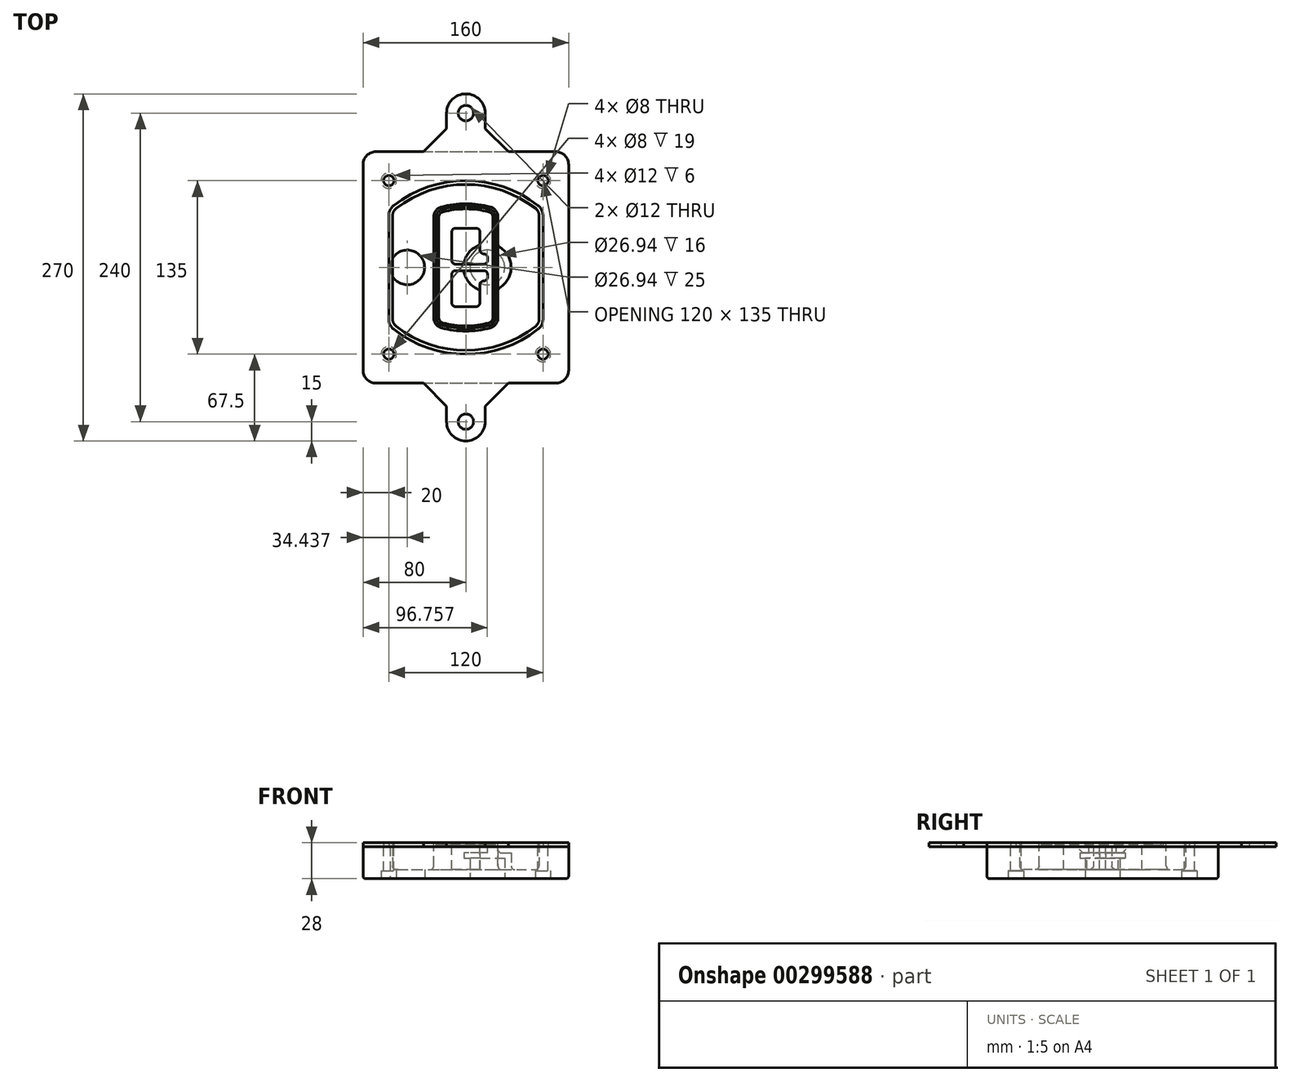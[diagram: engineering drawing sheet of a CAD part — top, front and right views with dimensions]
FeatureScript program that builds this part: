
annotation { "Feature Type Name" : "Feature", "Feature Type Description" : "" }
export const myFeature = defineFeature(function(context is Context, id is Id, definition is map)
    precondition{}
    {
        {
            var Q0;
            Q0=qCreatedBy(makeId("Top.planeOp"),FACE);
            var sketch = newSketch(context, id + "F0", { "sketchPlane" : qUnion([Q0])});
            skPoint(sketch, "E0.rect.middle", {"position": v(0, 0) * mm});
            skLineSegment(sketch, "E1.bottom", {"start": v(-70, -90) * mm, "end": v(70, -90) * mm});
            skLineSegment(sketch, "E1.top", {"start": v(-70, 90) * mm, "end": v(70, 90) * mm});
            skLineSegment(sketch, "E1.left", {"start": v(-80, -80) * mm, "end": v(-80, 80) * mm});
            skLineSegment(sketch, "E1.right", {"start": v(80, -80) * mm, "end": v(80, 80) * mm});
            skLineSegment(sketch, "E2", {"start": v(-80, 90) * mm, "end": v(80, -90) * mm, "construction": true});
            skLineSegment(sketch, "E3", {"start": v(80, 90) * mm, "end": v(-80, -90) * mm, "construction": true});
            skCircle(sketch, "E4", {"center": v(-60, 67.5) * mm, "radius": 4 * mm});
            skCircle(sketch, "E5", {"center": v(60, 67.5) * mm, "radius": 4 * mm});
            skCircle(sketch, "E6", {"center": v(60, -67.5) * mm, "radius": 4 * mm});
            skCircle(sketch, "E7", {"center": v(-60, -67.5) * mm, "radius": 4 * mm});
            skLineSegment(sketch, "E8", {"start": v(-60, 67.5) * mm, "end": v(60, 67.5) * mm, "construction": true});
            skLineSegment(sketch, "E9", {"start": v(60, 67.5) * mm, "end": v(60, -67.5) * mm, "construction": true});
            skLineSegment(sketch, "E10", {"start": v(60, -67.5) * mm, "end": v(-60, -67.5) * mm, "construction": true});
            skLineSegment(sketch, "E11", {"start": v(-60, -67.5) * mm, "end": v(-60, 67.5) * mm, "construction": true});
            skLineSegment(sketch, "E12", {"start": v(-60, 40.3) * mm, "end": v(-60, -40.3) * mm});
            skLineSegment(sketch, "E13", {"start": v(60, 40.3) * mm, "end": v(60, -40.3) * mm});
            skArc(sketch, "E14", {"start": v(56.15, 48.18) * mm, "mid": v(0, 67.5) * mm, "end": v(-56.15, 48.18) * mm});
            skArc(sketch, "E15", {"start": v(-56.15, -48.18) * mm, "mid": v(0, -67.5) * mm, "end": v(56.15, -48.18) * mm});
            skLineSegment(sketch, "E16", {"start": v(-60, 0) * mm, "end": v(60, 0) * mm, "construction": true});
            skPoint(sketch, "E17.visualSharp", {"position": v(-60, -45) * mm});
            skArc(sketch, "E17.filletArc", {"start": v(-60, -40.3) * mm, "mid": v(-58.99, -44.68) * mm, "end": v(-56.15, -48.18) * mm});
            skPoint(sketch, "E18.visualSharp", {"position": v(-60, 45) * mm});
            skArc(sketch, "E18.filletArc", {"start": v(-56.15, 48.18) * mm, "mid": v(-58.99, 44.68) * mm, "end": v(-60, 40.3) * mm});
            skPoint(sketch, "E19.visualSharp", {"position": v(60, 45) * mm});
            skArc(sketch, "E19.filletArc", {"start": v(60, 40.3) * mm, "mid": v(58.99, 44.68) * mm, "end": v(56.15, 48.18) * mm});
            skPoint(sketch, "E20.visualSharp", {"position": v(60, -45) * mm});
            skArc(sketch, "E20.filletArc", {"start": v(56.15, -48.18) * mm, "mid": v(58.99, -44.68) * mm, "end": v(60, -40.3) * mm});
            skPoint(sketch, "E21.visualSharp", {"position": v(-80, 90) * mm});
            skArc(sketch, "E21.filletArc", {"start": v(-70, 90) * mm, "mid": v(-77.07, 87.07) * mm, "end": v(-80, 80) * mm});
            skPoint(sketch, "E22.visualSharp", {"position": v(80, 90) * mm});
            skArc(sketch, "E22.filletArc", {"start": v(80, 80) * mm, "mid": v(77.07, 87.07) * mm, "end": v(70, 90) * mm});
            skPoint(sketch, "E23.visualSharp", {"position": v(80, -90) * mm});
            skArc(sketch, "E23.filletArc", {"start": v(70, -90) * mm, "mid": v(77.07, -87.07) * mm, "end": v(80, -80) * mm});
            skPoint(sketch, "E24.visualSharp", {"position": v(-80, -90) * mm});
            skArc(sketch, "E24.filletArc", {"start": v(-80, -80) * mm, "mid": v(-77.07, -87.07) * mm, "end": v(-70, -90) * mm});
            skArc(sketch, "E25.0", {"start": v(57, 40.3) * mm, "mid": v(56.3, 43.36) * mm, "end": v(54.3, 45.81) * mm});
            skLineSegment(sketch, "E25.1", {"start": v(57, 40.3) * mm, "end": v(57, -40.3) * mm});
            skArc(sketch, "E25.2", {"start": v(54.3, -45.81) * mm, "mid": v(56.3, -43.36) * mm, "end": v(57, -40.3) * mm});
            skArc(sketch, "E25.3", {"start": v(-54.3, -45.81) * mm, "mid": v(0, -64.5) * mm, "end": v(54.3, -45.81) * mm});
            skArc(sketch, "E25.4", {"start": v(-57, -40.3) * mm, "mid": v(-56.3, -43.36) * mm, "end": v(-54.3, -45.81) * mm});
            skArc(sketch, "E25.5", {"start": v(54.3, 45.81) * mm, "mid": v(0, 64.5) * mm, "end": v(-54.3, 45.81) * mm});
            skLineSegment(sketch, "E25.6", {"start": v(-57, 40.3) * mm, "end": v(-57, -40.3) * mm});
            skArc(sketch, "E25.7", {"start": v(-54.3, 45.81) * mm, "mid": v(-56.3, 43.36) * mm, "end": v(-57, 40.3) * mm});
            skArc(sketch, "E26.0", {"start": v(-58.62, 51.33) * mm, "mid": v(-62.58, 46.43) * mm, "end": v(-64, 40.3) * mm});
            skArc(sketch, "E26.1", {"start": v(58.62, 51.33) * mm, "mid": v(0, 71.5) * mm, "end": v(-58.62, 51.33) * mm});
            skArc(sketch, "E26.2", {"start": v(64, 40.3) * mm, "mid": v(62.58, 46.43) * mm, "end": v(58.62, 51.33) * mm});
            skLineSegment(sketch, "E26.3", {"start": v(64, 40.3) * mm, "end": v(64, -40.3) * mm});
            skArc(sketch, "E26.4", {"start": v(58.62, -51.33) * mm, "mid": v(62.58, -46.43) * mm, "end": v(64, -40.3) * mm});
            skLineSegment(sketch, "E26.5", {"start": v(-64, 40.3) * mm, "end": v(-64, -40.3) * mm});
            skArc(sketch, "E26.6", {"start": v(-58.62, -51.33) * mm, "mid": v(0, -71.5) * mm, "end": v(58.62, -51.33) * mm});
            skArc(sketch, "E26.7", {"start": v(-64, -40.3) * mm, "mid": v(-62.58, -46.43) * mm, "end": v(-58.62, -51.33) * mm});
            skSolve(sketch);
        }
        {
            var Q0;
            Q0=makeQuery(id+"F0.imprint","IMPRINT",FACE,{"disambiguationData":[TD([[makeQuery(id+"F0.imprint","IMPRINT",EDGE,{"derivedFrom":sQuery(id+"F0.wireOp",EDGE,"E1.bottom")}),1.0]])]});
            var Q1;
            Q1=makeQuery(id+"F0.imprint","IMPRINT",FACE,{"disambiguationData":[TD([[makeQuery(id+"F0.imprint","IMPRINT",EDGE,{"derivedFrom":sQuery(id+"F0.wireOp",EDGE,"E12")}),1.0]])]});
            var Q2;
            Q2=makeQuery(id+"F0.imprint","IMPRINT",FACE,{"disambiguationData":[TD([[makeQuery(id+"F0.imprint","IMPRINT",EDGE,{"derivedFrom":sQuery(id+"F0.wireOp",EDGE,"E25.0")}),1.0]])]});
            var Q3;
            Q3=makeQuery(id+"F0.imprint","IMPRINT",FACE,{"disambiguationData":[TD([[makeQuery(id+"F0.imprint","IMPRINT",EDGE,{"derivedFrom":sQuery(id+"F0.wireOp",EDGE,"E12")}),-1.0]])]});
            extrude(context, id + "F1", {"entities" : qUnion([Q0, Q1, Q2, Q3]), "oppositeDirection" : true, "depth" : 25 * mm});
        }
        {
            var Q0;
            Q0=makeQuery(id+"F0.imprint","IMPRINT",FACE,{"disambiguationData":[TD([[makeQuery(id+"F0.imprint","IMPRINT",EDGE,{"derivedFrom":sQuery(id+"F0.wireOp",EDGE,"E12")}),1.0]])]});
            extrude(context, id + "F2", {"entities" : qUnion([Q0]), "operationType" : NewBodyOperationType.ADD, "depth" : 3 * mm});
        }
        {
            var Q0;
            Q0=makeQuery(id+"F0.imprint","IMPRINT",FACE,{"disambiguationData":[TD([[makeQuery(id+"F0.imprint","IMPRINT",EDGE,{"derivedFrom":sQuery(id+"F0.wireOp",EDGE,"E25.0")}),1.0]])]});
            extrude(context, id + "F3", {"entities" : qUnion([Q0]), "operationType" : NewBodyOperationType.REMOVE, "oppositeDirection" : true, "depth" : 18 * mm});
        }
        {
            var Q0;
            Q0=makeQuery(id+"F2.opExtrude","CAP_FACE",FACE,{"disambiguationData":[OSD([sQuery(id+"F0.wireOp",EDGE,"E12"),sQuery(id+"F0.wireOp",EDGE,"E13"),sQuery(id+"F0.wireOp",EDGE,"E14"),sQuery(id+"F0.wireOp",EDGE,"E15"),sQuery(id+"F0.wireOp",EDGE,"E17.filletArc"),sQuery(id+"F0.wireOp",EDGE,"E18.filletArc"),sQuery(id+"F0.wireOp",EDGE,"E19.filletArc"),sQuery(id+"F0.wireOp",EDGE,"E20.filletArc"),sQuery(id+"F0.wireOp",EDGE,"E25.0"),sQuery(id+"F0.wireOp",EDGE,"E25.1"),sQuery(id+"F0.wireOp",EDGE,"E25.2"),sQuery(id+"F0.wireOp",EDGE,"E25.3"),sQuery(id+"F0.wireOp",EDGE,"E25.4"),sQuery(id+"F0.wireOp",EDGE,"E25.5"),sQuery(id+"F0.wireOp",EDGE,"E25.6"),sQuery(id+"F0.wireOp",EDGE,"E25.7")])],"isStart":false});
            var sketch = newSketch(context, id + "F4", { "sketchPlane" : qUnion([Q0])});
            skArc(sketch, "E27.0", {"start": v(-19.08, -46.97) * mm, "mid": v(0, -49.5) * mm, "end": v(19.08, -46.97) * mm});
            skArc(sketch, "E28.0", {"start": v(19.08, 46.97) * mm, "mid": v(0, 49.5) * mm, "end": v(-19.08, 46.97) * mm});
            skLineSegment(sketch, "E29", {"start": v(-25, 39.25) * mm, "end": v(-25, -39.25) * mm});
            skLineSegment(sketch, "E30", {"start": v(25, 39.25) * mm, "end": v(25, -39.25) * mm});
            skLineSegment(sketch, "E31", {"start": v(-25, 45.1) * mm, "end": v(25, 45.1) * mm, "construction": true});
            skLineSegment(sketch, "E32", {"start": v(-25, -45.1) * mm, "end": v(25, -45.1) * mm, "construction": true});
            skPoint(sketch, "E33.visualSharp", {"position": v(-25, 45.1) * mm});
            skArc(sketch, "E33.filletArc", {"start": v(-19.08, 46.97) * mm, "mid": v(-23.35, 44.11) * mm, "end": v(-25, 39.25) * mm});
            skPoint(sketch, "E34.visualSharp", {"position": v(25, 45.1) * mm});
            skArc(sketch, "E34.filletArc", {"start": v(25, 39.25) * mm, "mid": v(23.35, 44.11) * mm, "end": v(19.08, 46.97) * mm});
            skPoint(sketch, "E35.visualSharp", {"position": v(25, -45.1) * mm});
            skArc(sketch, "E35.filletArc", {"start": v(19.08, -46.97) * mm, "mid": v(23.35, -44.11) * mm, "end": v(25, -39.25) * mm});
            skPoint(sketch, "E36.visualSharp", {"position": v(-25, -45.1) * mm});
            skArc(sketch, "E36.filletArc", {"start": v(-25, -39.25) * mm, "mid": v(-23.35, -44.11) * mm, "end": v(-19.08, -46.97) * mm});
            skArc(sketch, "E37.0", {"start": v(54.3, 45.81) * mm, "mid": v(0, 64.5) * mm, "end": v(-54.3, 45.81) * mm});
            skArc(sketch, "E37.1", {"start": v(-54.3, 45.81) * mm, "mid": v(-56.3, 43.36) * mm, "end": v(-57, 40.3) * mm});
            skLineSegment(sketch, "E37.2", {"start": v(-57, 40.3) * mm, "end": v(-57, -40.3) * mm});
            skArc(sketch, "E37.3", {"start": v(-57, -40.3) * mm, "mid": v(-56.3, -43.36) * mm, "end": v(-54.3, -45.81) * mm});
            skArc(sketch, "E37.4", {"start": v(-54.3, -45.81) * mm, "mid": v(0, -64.5) * mm, "end": v(54.3, -45.81) * mm});
            skArc(sketch, "E37.5", {"start": v(54.3, -45.81) * mm, "mid": v(56.3, -43.36) * mm, "end": v(57, -40.3) * mm});
            skLineSegment(sketch, "E37.6", {"start": v(57, 40.3) * mm, "end": v(57, -40.3) * mm});
            skArc(sketch, "E37.7", {"start": v(57, 40.3) * mm, "mid": v(56.3, 43.36) * mm, "end": v(54.3, 45.81) * mm});
            skLineSegment(sketch, "E38.0", {"start": v(23, 39.25) * mm, "end": v(23, -39.25) * mm});
            skArc(sketch, "E38.1", {"start": v(18.56, -45.04) * mm, "mid": v(21.76, -42.9) * mm, "end": v(23, -39.25) * mm});
            skArc(sketch, "E38.2", {"start": v(-18.56, -45.04) * mm, "mid": v(0, -47.5) * mm, "end": v(18.56, -45.04) * mm});
            skArc(sketch, "E38.3", {"start": v(-23, -39.25) * mm, "mid": v(-21.76, -42.9) * mm, "end": v(-18.56, -45.04) * mm});
            skLineSegment(sketch, "E38.4", {"start": v(-23, 39.25) * mm, "end": v(-23, -39.25) * mm});
            skArc(sketch, "E38.5", {"start": v(23, 39.25) * mm, "mid": v(21.76, 42.9) * mm, "end": v(18.56, 45.04) * mm});
            skArc(sketch, "E38.6", {"start": v(-18.56, 45.04) * mm, "mid": v(-21.76, 42.9) * mm, "end": v(-23, 39.25) * mm});
            skArc(sketch, "E38.7", {"start": v(18.56, 45.04) * mm, "mid": v(0, 47.5) * mm, "end": v(-18.56, 45.04) * mm});
            skArc(sketch, "E39.0", {"start": v(21, 39.25) * mm, "mid": v(20.18, 41.68) * mm, "end": v(18.04, 43.1) * mm});
            skLineSegment(sketch, "E39.1", {"start": v(21, 39.25) * mm, "end": v(21, -39.25) * mm});
            skArc(sketch, "E39.2", {"start": v(18.04, -43.1) * mm, "mid": v(20.18, -41.68) * mm, "end": v(21, -39.25) * mm});
            skArc(sketch, "E39.3", {"start": v(-18.04, -43.1) * mm, "mid": v(0, -45.5) * mm, "end": v(18.04, -43.1) * mm});
            skArc(sketch, "E39.4", {"start": v(-21, -39.25) * mm, "mid": v(-20.18, -41.68) * mm, "end": v(-18.04, -43.1) * mm});
            skArc(sketch, "E39.5", {"start": v(18.04, 43.1) * mm, "mid": v(0, 45.5) * mm, "end": v(-18.04, 43.1) * mm});
            skLineSegment(sketch, "E39.6", {"start": v(-21, 39.25) * mm, "end": v(-21, -39.25) * mm});
            skArc(sketch, "E39.7", {"start": v(-18.04, 43.1) * mm, "mid": v(-20.18, 41.68) * mm, "end": v(-21, 39.25) * mm});
            skLineSegment(sketch, "E40", {"start": v(-25, 0) * mm, "end": v(25, 0) * mm, "construction": true});
            skLineSegment(sketch, "E41", {"start": v(-11, 5.5) * mm, "end": v(-11, 27.5) * mm});
            skLineSegment(sketch, "E42", {"start": v(-8, 30.5) * mm, "end": v(8, 30.5) * mm});
            skLineSegment(sketch, "E43", {"start": v(11, 27.5) * mm, "end": v(11, 13.5) * mm});
            skLineSegment(sketch, "E44", {"start": v(14, 10.5) * mm, "end": v(14, 10.5) * mm});
            skLineSegment(sketch, "E45", {"start": v(17, 7.5) * mm, "end": v(17, 5.5) * mm});
            skLineSegment(sketch, "E46", {"start": v(14, 2.5) * mm, "end": v(-8, 2.5) * mm});
            skPoint(sketch, "E47.visualSharp", {"position": v(-11, 30.5) * mm});
            skArc(sketch, "E47.filletArc", {"start": v(-8, 30.5) * mm, "mid": v(-10.12, 29.62) * mm, "end": v(-11, 27.5) * mm});
            skPoint(sketch, "E48.visualSharp", {"position": v(11, 30.5) * mm});
            skArc(sketch, "E48.filletArc", {"start": v(11, 27.5) * mm, "mid": v(10.12, 29.62) * mm, "end": v(8, 30.5) * mm});
            skPoint(sketch, "E49.visualSharp", {"position": v(11, 10.5) * mm});
            skArc(sketch, "E49.filletArc", {"start": v(11, 13.5) * mm, "mid": v(11.88, 11.38) * mm, "end": v(14, 10.5) * mm});
            skPoint(sketch, "E50.visualSharp", {"position": v(17, 10.5) * mm});
            skArc(sketch, "E50.filletArc", {"start": v(17, 7.5) * mm, "mid": v(16.12, 9.62) * mm, "end": v(14, 10.5) * mm});
            skPoint(sketch, "E51.visualSharp", {"position": v(17, 2.5) * mm});
            skArc(sketch, "E51.filletArc", {"start": v(14, 2.5) * mm, "mid": v(16.12, 3.38) * mm, "end": v(17, 5.5) * mm});
            skPoint(sketch, "E52.visualSharp", {"position": v(-11, 2.5) * mm});
            skArc(sketch, "E52.filletArc", {"start": v(-11, 5.5) * mm, "mid": v(-10.12, 3.38) * mm, "end": v(-8, 2.5) * mm});
            skLineSegment(sketch, "E53.0.MirrorCS", {"start": v(14, -2.5) * mm, "end": v(-8, -2.5) * mm});
            skArc(sketch, "E54.0.MirrorCS", {"start": v(-11, -5.5) * mm, "mid": v(-10.12, -3.38) * mm, "end": v(-8, -2.5) * mm});
            skLineSegment(sketch, "E55.0.MirrorCS", {"start": v(-11, -5.5) * mm, "end": v(-11, -27.5) * mm});
            skArc(sketch, "E56.0.MirrorCS", {"start": v(-8, -30.5) * mm, "mid": v(-10.12, -29.62) * mm, "end": v(-11, -27.5) * mm});
            skLineSegment(sketch, "E57.0.MirrorCS", {"start": v(-8, -30.5) * mm, "end": v(8, -30.5) * mm});
            skArc(sketch, "E58.0.MirrorCS", {"start": v(11, -27.5) * mm, "mid": v(10.12, -29.62) * mm, "end": v(8, -30.5) * mm});
            skLineSegment(sketch, "E59.0.MirrorCS", {"start": v(11, -27.5) * mm, "end": v(11, -13.5) * mm});
            skArc(sketch, "E60.0.MirrorCS", {"start": v(11, -13.5) * mm, "mid": v(11.88, -11.38) * mm, "end": v(14, -10.5) * mm});
            skArc(sketch, "E61.0.MirrorCS", {"start": v(17, -7.5) * mm, "mid": v(16.12, -9.62) * mm, "end": v(14, -10.5) * mm});
            skLineSegment(sketch, "E62.0.MirrorCS", {"start": v(17, -7.5) * mm, "end": v(17, -5.5) * mm});
            skArc(sketch, "E63.0.MirrorCS", {"start": v(14, -2.5) * mm, "mid": v(16.12, -3.38) * mm, "end": v(17, -5.5) * mm});
            skSolve(sketch);
        }
        {
            var Q0;
            Q0=makeQuery(id+"F4.imprint","IMPRINT",FACE,{"disambiguationData":[TD([[makeQuery(id+"F4.imprint","IMPRINT",EDGE,{"derivedFrom":sQuery(id+"F4.wireOp",EDGE,"E27.0")}),1.0]])]});
            var Q1;
            Q1=makeQuery(id+"F4.imprint","IMPRINT",FACE,{"disambiguationData":[TD([[makeQuery(id+"F4.imprint","IMPRINT",EDGE,{"derivedFrom":sQuery(id+"F4.wireOp",EDGE,"E38.0")}),-1.0]])]});
            var Q2;
            Q2=makeQuery(id+"F4.imprint","IMPRINT",FACE,{"disambiguationData":[TD([[makeQuery(id+"F4.imprint","IMPRINT",EDGE,{"derivedFrom":sQuery(id+"F4.wireOp",EDGE,"E39.0")}),1.0]])]});
            extrude(context, id + "F5", {"entities" : qUnion([Q0, Q1, Q2]), "operationType" : NewBodyOperationType.ADD, "endBound" : BoundingType.UP_TO_NEXT, "oppositeDirection" : true, "depth" : 25 * mm});
        }
        {
            var Q0;
            Q0=makeQuery(id+"F4.imprint","IMPRINT",FACE,{"disambiguationData":[TD([[makeQuery(id+"F4.imprint","IMPRINT",EDGE,{"derivedFrom":sQuery(id+"F4.wireOp",EDGE,"E38.0")}),-1.0]])]});
            extrude(context, id + "F6", {"entities" : qUnion([Q0]), "operationType" : NewBodyOperationType.REMOVE, "oppositeDirection" : true, "depth" : 2 * mm});
        }
        {
            var Q0;
            Q0=makeQuery(id+"F1.opExtrude","CAP_FACE",FACE,{"disambiguationData":[OSD([sQuery(id+"F0.wireOp",EDGE,"E1.bottom"),sQuery(id+"F0.wireOp",EDGE,"E1.top"),sQuery(id+"F0.wireOp",EDGE,"E1.left"),sQuery(id+"F0.wireOp",EDGE,"E1.right"),sQuery(id+"F0.wireOp",EDGE,"E4"),sQuery(id+"F0.wireOp",EDGE,"E5"),sQuery(id+"F0.wireOp",EDGE,"E6"),sQuery(id+"F0.wireOp",EDGE,"E7"),sQuery(id+"F0.wireOp",EDGE,"E21.filletArc"),sQuery(id+"F0.wireOp",EDGE,"E22.filletArc"),sQuery(id+"F0.wireOp",EDGE,"E23.filletArc"),sQuery(id+"F0.wireOp",EDGE,"E24.filletArc")])],"isStart":false});
            var sketch = newSketch(context, id + "F7", { "sketchPlane" : qUnion([Q0])});
            skCircle(sketch, "E64", {"center": v(16.76, 0) * mm, "radius": 13.47 * mm});
            skCircle(sketch, "E65", {"center": v(-45.56, 0) * mm, "radius": 13.47 * mm});
            skLineSegment(sketch, "E66", {"start": v(80, 0) * mm, "end": v(-80, 0) * mm});
            skCircle(sketch, "E67", {"center": v(16.76, 0) * mm, "radius": 18.47 * mm});
            skCircle(sketch, "E68", {"center": v(60, -67.5) * mm, "radius": 6 * mm});
            skCircle(sketch, "E69", {"center": v(-60, -67.5) * mm, "radius": 6 * mm});
            skCircle(sketch, "E70", {"center": v(-60, 67.5) * mm, "radius": 6 * mm});
            skCircle(sketch, "E71", {"center": v(60, 67.5) * mm, "radius": 6 * mm});
            skSolve(sketch);
        }
        {
            var Q0;
            {var subQ1=sQuery(id+"F7.wireOp",EDGE,"E66");var subQ4=sQuery(id+"F7.wireOp",EDGE,"E64");var subQ6=makeQuery(id+"F7.imprint","INTERSECT",VERTEX,{"disambiguationData":[OD(0.0)],"derivedFrom":[subQ4,subQ1]});Q0=makeQuery(id+"F7.imprint","IMPRINT",FACE,{"disambiguationData":[TD([[makeQuery(id+"F7.imprint","IMPRINT",EDGE,{"disambiguationData":[TD([[subQ6,-1.0]])],"derivedFrom":subQ4}),-1.0]])]});}
            var Q1;
            {var subQ0=sQuery(id+"F7.wireOp",EDGE,"E66");var subQ1=sQuery(id+"F7.wireOp",EDGE,"E64");var subQ3=makeQuery(id+"F7.imprint","INTERSECT",VERTEX,{"disambiguationData":[OD(0.0)],"derivedFrom":[subQ1,subQ0]});Q1=makeQuery(id+"F7.imprint","IMPRINT",FACE,{"disambiguationData":[TD([[makeQuery(id+"F7.imprint","IMPRINT",EDGE,{"disambiguationData":[TD([[subQ3,-1.0]])],"derivedFrom":subQ1}),1.0]])]});}
            var Q2;
            {var subQ0=sQuery(id+"F7.wireOp",EDGE,"E66");var subQ1=sQuery(id+"F7.wireOp",EDGE,"E64");var subQ3=makeQuery(id+"F7.imprint","INTERSECT",VERTEX,{"disambiguationData":[OD(0.0)],"derivedFrom":[subQ1,subQ0]});Q2=makeQuery(id+"F7.imprint","IMPRINT",FACE,{"disambiguationData":[TD([[makeQuery(id+"F7.imprint","IMPRINT",EDGE,{"disambiguationData":[TD([[subQ3,1.0]])],"derivedFrom":subQ1}),1.0]])]});}
            var Q3;
            {var subQ1=sQuery(id+"F7.wireOp",EDGE,"E66");var subQ4=sQuery(id+"F7.wireOp",EDGE,"E64");var subQ6=makeQuery(id+"F7.imprint","INTERSECT",VERTEX,{"disambiguationData":[OD(0.0)],"derivedFrom":[subQ4,subQ1]});Q3=makeQuery(id+"F7.imprint","IMPRINT",FACE,{"disambiguationData":[TD([[makeQuery(id+"F7.imprint","IMPRINT",EDGE,{"disambiguationData":[TD([[subQ6,1.0]])],"derivedFrom":subQ4}),-1.0]])]});}
            extrude(context, id + "F8", {"entities" : qUnion([Q0, Q1, Q2, Q3]), "operationType" : NewBodyOperationType.ADD, "oppositeDirection" : true, "depth" : 20 * mm});
        }
        {
            var Q0;
            {var subQ0=sQuery(id+"F7.wireOp",EDGE,"E66");var subQ1=sQuery(id+"F7.wireOp",EDGE,"E64");var subQ3=makeQuery(id+"F7.imprint","INTERSECT",VERTEX,{"disambiguationData":[OD(0.0)],"derivedFrom":[subQ1,subQ0]});Q0=makeQuery(id+"F7.imprint","IMPRINT",FACE,{"disambiguationData":[TD([[makeQuery(id+"F7.imprint","IMPRINT",EDGE,{"disambiguationData":[TD([[subQ3,-1.0]])],"derivedFrom":subQ1}),1.0]])]});}
            var Q1;
            {var subQ0=sQuery(id+"F7.wireOp",EDGE,"E66");var subQ1=sQuery(id+"F7.wireOp",EDGE,"E64");var subQ3=makeQuery(id+"F7.imprint","INTERSECT",VERTEX,{"disambiguationData":[OD(0.0)],"derivedFrom":[subQ1,subQ0]});Q1=makeQuery(id+"F7.imprint","IMPRINT",FACE,{"disambiguationData":[TD([[makeQuery(id+"F7.imprint","IMPRINT",EDGE,{"disambiguationData":[TD([[subQ3,1.0]])],"derivedFrom":subQ1}),1.0]])]});}
            extrude(context, id + "F9", {"entities" : qUnion([Q0, Q1]), "operationType" : NewBodyOperationType.REMOVE, "oppositeDirection" : true, "depth" : 16 * mm});
        }
        {
            var Q0;
            {var subQ0=sQuery(id+"F7.wireOp",EDGE,"E66");var subQ1=sQuery(id+"F7.wireOp",EDGE,"E65");var subQ3=makeQuery(id+"F7.imprint","INTERSECT",VERTEX,{"disambiguationData":[OD(0.0)],"derivedFrom":[subQ1,subQ0]});Q0=makeQuery(id+"F7.imprint","IMPRINT",FACE,{"disambiguationData":[TD([[makeQuery(id+"F7.imprint","IMPRINT",EDGE,{"disambiguationData":[TD([[subQ3,-1.0]])],"derivedFrom":subQ1}),1.0]])]});}
            var Q1;
            {var subQ0=sQuery(id+"F7.wireOp",EDGE,"E66");var subQ1=sQuery(id+"F7.wireOp",EDGE,"E65");var subQ3=makeQuery(id+"F7.imprint","INTERSECT",VERTEX,{"disambiguationData":[OD(0.0)],"derivedFrom":[subQ1,subQ0]});Q1=makeQuery(id+"F7.imprint","IMPRINT",FACE,{"disambiguationData":[TD([[makeQuery(id+"F7.imprint","IMPRINT",EDGE,{"disambiguationData":[TD([[subQ3,1.0]])],"derivedFrom":subQ1}),1.0]])]});}
            extrude(context, id + "F10", {"entities" : qUnion([Q0, Q1]), "operationType" : NewBodyOperationType.REMOVE, "oppositeDirection" : true, "depth" : 25 * mm});
        }
        {
            var Q0;
            Q0=makeQuery(id+"F7.imprint","IMPRINT",FACE,{"disambiguationData":[TD([[makeQuery(id+"F7.imprint","IMPRINT",EDGE,{"derivedFrom":sQuery(id+"F7.wireOp",EDGE,"E68")}),1.0]])]});
            var Q1;
            Q1=makeQuery(id+"F7.imprint","IMPRINT",FACE,{"disambiguationData":[TD([[makeQuery(id+"F7.imprint","IMPRINT",EDGE,{"derivedFrom":makeQuery(id+"F1.opExtrude","CAP_EDGE",EDGE,{"disambiguationData":[OSD([sQuery(id+"F0.wireOp",EDGE,"E5")])],"isStart":false})}),-1.0]])]});
            var Q2;
            Q2=makeQuery(id+"F7.imprint","IMPRINT",FACE,{"disambiguationData":[TD([[makeQuery(id+"F7.imprint","IMPRINT",EDGE,{"derivedFrom":sQuery(id+"F7.wireOp",EDGE,"E69")}),1.0]])]});
            var Q3;
            Q3=makeQuery(id+"F7.imprint","IMPRINT",FACE,{"disambiguationData":[TD([[makeQuery(id+"F7.imprint","IMPRINT",EDGE,{"derivedFrom":makeQuery(id+"F1.opExtrude","CAP_EDGE",EDGE,{"disambiguationData":[OSD([sQuery(id+"F0.wireOp",EDGE,"E4")])],"isStart":false})}),-1.0]])]});
            var Q4;
            Q4=makeQuery(id+"F7.imprint","IMPRINT",FACE,{"disambiguationData":[TD([[makeQuery(id+"F7.imprint","IMPRINT",EDGE,{"derivedFrom":sQuery(id+"F7.wireOp",EDGE,"E70")}),1.0]])]});
            var Q5;
            Q5=makeQuery(id+"F7.imprint","IMPRINT",FACE,{"disambiguationData":[TD([[makeQuery(id+"F7.imprint","IMPRINT",EDGE,{"derivedFrom":makeQuery(id+"F1.opExtrude","CAP_EDGE",EDGE,{"disambiguationData":[OSD([sQuery(id+"F0.wireOp",EDGE,"E7")])],"isStart":false})}),-1.0]])]});
            var Q6;
            Q6=makeQuery(id+"F7.imprint","IMPRINT",FACE,{"disambiguationData":[TD([[makeQuery(id+"F7.imprint","IMPRINT",EDGE,{"derivedFrom":sQuery(id+"F7.wireOp",EDGE,"E71")}),1.0]])]});
            var Q7;
            Q7=makeQuery(id+"F7.imprint","IMPRINT",FACE,{"disambiguationData":[TD([[makeQuery(id+"F7.imprint","IMPRINT",EDGE,{"derivedFrom":makeQuery(id+"F1.opExtrude","CAP_EDGE",EDGE,{"disambiguationData":[OSD([sQuery(id+"F0.wireOp",EDGE,"E6")])],"isStart":false})}),-1.0]])]});
            extrude(context, id + "F11", {"entities" : qUnion([Q0, Q1, Q2, Q3, Q4, Q5, Q6, Q7]), "operationType" : NewBodyOperationType.REMOVE, "oppositeDirection" : true, "depth" : 6 * mm});
        }
        {
            var Q0;
            Q0=makeQuery(id+"F9.boolean.opBoolean","COPY",FACE,{"derivedFrom":makeQuery(id+"F9.opExtrude","CAP_FACE",FACE,{"disambiguationData":[OSD([sQuery(id+"F7.wireOp",EDGE,"E64")])],"isStart":false})});
            var sketch = newSketch(context, id + "F12", { "sketchPlane" : qUnion([Q0])});
            skArc(sketch, "E72.0", {"start": v(11, 17.55) * mm, "mid": v(2.57, 11.82) * mm, "end": v(-1.54, 2.5) * mm});
            skArc(sketch, "E72.1", {"start": v(-1.54, -2.5) * mm, "mid": v(2.57, -11.82) * mm, "end": v(11, -17.55) * mm});
            skLineSegment(sketch, "E73", {"start": v(-1.54, -2.5) * mm, "end": v(14, -2.5) * mm});
            skLineSegment(sketch, "E74.0", {"start": v(14, 2.5) * mm, "end": v(-1.54, 2.5) * mm});
            skArc(sketch, "E74.1", {"start": v(14, 2.5) * mm, "mid": v(16.12, 3.38) * mm, "end": v(17, 5.5) * mm});
            skLineSegment(sketch, "E74.2", {"start": v(17, 7.5) * mm, "end": v(17, 5.5) * mm});
            skArc(sketch, "E74.3", {"start": v(17, 7.5) * mm, "mid": v(16.12, 9.62) * mm, "end": v(14, 10.5) * mm});
            skArc(sketch, "E74.4", {"start": v(11, 13.5) * mm, "mid": v(11.88, 11.38) * mm, "end": v(14, 10.5) * mm});
            skLineSegment(sketch, "E74.5", {"start": v(11, 17.55) * mm, "end": v(11, 13.5) * mm});
            skLineSegment(sketch, "E74.7", {"start": v(14, -2.5) * mm, "end": v(-1.54, -2.5) * mm});
            skArc(sketch, "E74.8", {"start": v(14, -2.5) * mm, "mid": v(16.12, -3.38) * mm, "end": v(17, -5.5) * mm});
            skLineSegment(sketch, "E74.9", {"start": v(17, -7.5) * mm, "end": v(17, -5.5) * mm});
            skArc(sketch, "E74.10", {"start": v(17, -7.5) * mm, "mid": v(16.12, -9.62) * mm, "end": v(14, -10.5) * mm});
            skArc(sketch, "E74.11", {"start": v(11, -13.5) * mm, "mid": v(11.88, -11.38) * mm, "end": v(14, -10.5) * mm});
            skLineSegment(sketch, "E74.12", {"start": v(11, -17.55) * mm, "end": v(11, -13.5) * mm});
            skPoint(sketch, "E75.orphan", {"position": v(11, -27.5) * mm});
            skPoint(sketch, "E76.orphan", {"position": v(-8, -2.5) * mm});
            skPoint(sketch, "E77.orphan", {"position": v(-8, 2.5) * mm});
            skPoint(sketch, "E78.orphan", {"position": v(11, 27.5) * mm});
            skSolve(sketch);
        }
        {
            var Q0;
            {var subQ7=sQuery(id+"F12.wireOp",EDGE,"E72.0");var subQ14=sQuery(id+"F12.wireOp",EDGE,"E72.1");var subQ16=sQuery(id+"F12.wireOp",EDGE,"E74.1");var subQ18=sQuery(id+"F12.wireOp",EDGE,"E74.8");Q0=qUnion([makeQuery(id+"F12.imprint","IMPRINT",FACE,{"disambiguationData":[TD([[makeQuery(id+"F12.imprint","IMPRINT",EDGE,{"derivedFrom":subQ7}),1.0]])]}),makeQuery(id+"F12.imprint","IMPRINT",FACE,{"disambiguationData":[TD([[makeQuery(id+"F12.imprint","IMPRINT",EDGE,{"derivedFrom":subQ14}),1.0]])]}),makeQuery(id+"F12.imprint","IMPRINT",FACE,{"disambiguationData":[TD([[makeQuery(id+"F12.imprint","IMPRINT",EDGE,{"derivedFrom":subQ16}),1.0]])]}),makeQuery(id+"F12.imprint","IMPRINT",FACE,{"disambiguationData":[TD([[makeQuery(id+"F12.imprint","IMPRINT",EDGE,{"derivedFrom":subQ18}),-1.0]])]})]);}
            var Q1;
            Q1=makeQuery(id+"F5.boolean.opBoolean","SPLIT",FACE,{"disambiguationData":[TD([makeQuery(id+"F5.opExtrude","SWEPT_FACE",FACE,{"disambiguationData":[OSD([sQuery(id+"F4.wireOp",EDGE,"E41")])]})])],"derivedFrom":makeQuery(id+"F3.boolean.opBoolean","COPY",FACE,{"derivedFrom":makeQuery(id+"F3.opExtrude","CAP_FACE",FACE,{"disambiguationData":[OSD([sQuery(id+"F0.wireOp",EDGE,"E25.0"),sQuery(id+"F0.wireOp",EDGE,"E25.1"),sQuery(id+"F0.wireOp",EDGE,"E25.2"),sQuery(id+"F0.wireOp",EDGE,"E25.3"),sQuery(id+"F0.wireOp",EDGE,"E25.4"),sQuery(id+"F0.wireOp",EDGE,"E25.5"),sQuery(id+"F0.wireOp",EDGE,"E25.6"),sQuery(id+"F0.wireOp",EDGE,"E25.7")])],"isStart":false})})});
            extrude(context, id + "F13", {"entities" : qUnion([Q0]), "operationType" : NewBodyOperationType.REMOVE, "endBound" : BoundingType.UP_TO_SURFACE, "endBoundEntityFace" : qUnion([Q1]), "depth" : 25 * mm});
        }
        {
            var Q0;
            Q0=makeQuery(id+"F3.boolean.opBoolean","COPY",EDGE,{"derivedFrom":makeQuery(id+"F3.opExtrude","CAP_EDGE",EDGE,{"disambiguationData":[OSD([sQuery(id+"F0.wireOp",EDGE,"E25.6")])],"isStart":false})});
            var Q1;
            Q1=makeQuery(id+"F8.boolean.opBoolean","INTERSECT",EDGE,{"derivedFrom":[makeQuery(id+"F5.opExtrude","SWEPT_FACE",FACE,{"disambiguationData":[OSD([sQuery(id+"F4.wireOp",EDGE,"E30")])]}),makeQuery(id+"F8.opExtrude","CAP_FACE",FACE,{"disambiguationData":[OSD([sQuery(id+"F7.wireOp",EDGE,"E67")])],"isStart":false})]});
            var Q2;
            Q2=makeQuery(id+"F8.boolean.opBoolean","INTERSECT",EDGE,{"disambiguationData":[OD(1.0)],"derivedFrom":[makeQuery(id+"F5.opExtrude","SWEPT_FACE",FACE,{"disambiguationData":[OSD([sQuery(id+"F4.wireOp",EDGE,"E30")])]}),makeQuery(id+"F8.opExtrude","SWEPT_FACE",FACE,{"disambiguationData":[OSD([sQuery(id+"F7.wireOp",EDGE,"E67")])]})]});
            var Q3;
            {var subQ0=sQuery(id+"F4.wireOp",EDGE,"E30");Q3=makeQuery(id+"F8.boolean.opBoolean","SPLIT",EDGE,{"disambiguationData":[TD([makeQuery(id+"F5.opExtrude","SWEPT_FACE",FACE,{"disambiguationData":[OSD([sQuery(id+"F4.wireOp",EDGE,"E35.filletArc")])]})])],"derivedFrom":makeQuery(id+"F5.opExtrude","CAP_EDGE",EDGE,{"disambiguationData":[OSD([subQ0])],"isStart":false})});}
            var Q4;
            {var subQ0=sQuery(id+"F0.wireOp",EDGE,"E25.7");var subQ1=sQuery(id+"F0.wireOp",EDGE,"E25.1");var subQ2=sQuery(id+"F0.wireOp",EDGE,"E25.6");var subQ3=sQuery(id+"F0.wireOp",EDGE,"E25.5");var subQ4=sQuery(id+"F0.wireOp",EDGE,"E25.4");var subQ5=sQuery(id+"F0.wireOp",EDGE,"E25.0");var subQ6=sQuery(id+"F0.wireOp",EDGE,"E25.2");var subQ7=sQuery(id+"F0.wireOp",EDGE,"E25.3");Q4=makeQuery(id+"F8.boolean.opBoolean","INTERSECT",EDGE,{"derivedFrom":[makeQuery(id+"F5.boolean.opBoolean","SPLIT",FACE,{"disambiguationData":[TD([makeQuery(id+"F2.opExtrude","SWEPT_FACE",FACE,{"disambiguationData":[OSD([subQ5])]})])],"derivedFrom":makeQuery(id+"F3.boolean.opBoolean","COPY",FACE,{"derivedFrom":makeQuery(id+"F3.opExtrude","CAP_FACE",FACE,{"disambiguationData":[OSD([subQ5,subQ1,subQ6,subQ7,subQ4,subQ3,subQ2,subQ0])],"isStart":false})})}),makeQuery(id+"F8.opExtrude","SWEPT_FACE",FACE,{"disambiguationData":[OSD([sQuery(id+"F7.wireOp",EDGE,"E67")])]})]});}
            var Q5;
            Q5=makeQuery(id+"F8.boolean.opBoolean","INTERSECT",EDGE,{"disambiguationData":[OD(0.0)],"derivedFrom":[makeQuery(id+"F5.opExtrude","SWEPT_FACE",FACE,{"disambiguationData":[OSD([sQuery(id+"F4.wireOp",EDGE,"E30")])]}),makeQuery(id+"F8.opExtrude","SWEPT_FACE",FACE,{"disambiguationData":[OSD([sQuery(id+"F7.wireOp",EDGE,"E67")])]})]});
            fillet(context, id + "F14", {"entities" : qUnion([Q0, Q1, Q2, Q3, Q4, Q5]), "radius" : 3 * mm, "tangentPropagation" : true, "allowEdgeOverflow" : false});
        }
        {
            var Q0;
            Q0=makeQuery(id+"F1.opExtrude","CAP_EDGE",EDGE,{"disambiguationData":[OSD([sQuery(id+"F0.wireOp",EDGE,"E1.bottom")])],"isStart":false});
            fillet(context, id + "F15", {"entities" : qUnion([Q0]), "radius" : 2 * mm, "tangentPropagation" : true, "allowEdgeOverflow" : false});
        }
        {
            var Q0;
            {var subQ0=sQuery(id+"F0.wireOp",EDGE,"E21.filletArc");var subQ1=sQuery(id+"F0.wireOp",EDGE,"E7");var subQ2=sQuery(id+"F0.wireOp",EDGE,"E6");var subQ3=sQuery(id+"F0.wireOp",EDGE,"E5");var subQ4=sQuery(id+"F0.wireOp",EDGE,"E4");var subQ5=sQuery(id+"F0.wireOp",EDGE,"E22.filletArc");var subQ6=sQuery(id+"F0.wireOp",EDGE,"E1.bottom");var subQ7=sQuery(id+"F0.wireOp",EDGE,"E1.right");var subQ8=sQuery(id+"F0.wireOp",EDGE,"E1.top");var subQ9=sQuery(id+"F0.wireOp",EDGE,"E1.left");var subQ10=sQuery(id+"F0.wireOp",EDGE,"E23.filletArc");var subQ11=sQuery(id+"F0.wireOp",EDGE,"E24.filletArc");Q0=makeQuery(id+"F2.boolean.opBoolean","SPLIT",FACE,{"disambiguationData":[TD([makeQuery(id+"F1.opExtrude","SWEPT_FACE",FACE,{"disambiguationData":[OSD([subQ6])]})])],"derivedFrom":makeQuery(id+"F1.opExtrude","CAP_FACE",FACE,{"disambiguationData":[OSD([subQ6,subQ8,subQ9,subQ7,subQ4,subQ3,subQ2,subQ1,subQ0,subQ5,subQ10,subQ11])],"isStart":true})});}
            var sketch = newSketch(context, id + "F16", { "sketchPlane" : qUnion([Q0])});
            skLineSegment(sketch, "E79", {"start": v(0, 90) * mm, "end": v(0, 120) * mm, "construction": true});
            skPoint(sketch, "E79.endSnap0", {"position": v(0, 90) * mm});
            skCircle(sketch, "E80", {"center": v(0, 120) * mm, "radius": 6 * mm});
            skArc(sketch, "E81", {"start": v(15, 120) * mm, "mid": v(0, 135) * mm, "end": v(-15, 120) * mm});
            skLineSegment(sketch, "E82", {"start": v(-15, 120) * mm, "end": v(-15, 108) * mm});
            skLineSegment(sketch, "E83", {"start": v(-15, 108) * mm, "end": v(-33, 90) * mm});
            skLineSegment(sketch, "E84", {"start": v(15, 120) * mm, "end": v(15, 108) * mm});
            skLineSegment(sketch, "E85", {"start": v(15, 108) * mm, "end": v(33, 90) * mm});
            skLineSegment(sketch, "E86", {"start": v(-80, 0) * mm, "end": v(80, 0) * mm, "construction": true});
            skArc(sketch, "E87.MirrorCS", {"start": v(-15, 120) * mm, "mid": v(0, 135) * mm, "end": v(15, 120) * mm});
            skLineSegment(sketch, "E88.MirrorCS", {"start": v(15, -120) * mm, "end": v(15, -108) * mm});
            skCircle(sketch, "E89.MirrorC", {"center": v(0, -120) * mm, "radius": 6 * mm});
            skArc(sketch, "E90.MirrorCS", {"start": v(15, -120) * mm, "mid": v(0, -135) * mm, "end": v(-15, -120) * mm});
            skPoint(sketch, "E91.MirrorP", {"position": v(0, -90) * mm});
            skLineSegment(sketch, "E92.MirrorCS", {"start": v(-15, -108) * mm, "end": v(-33, -90) * mm});
            skLineSegment(sketch, "E93.MirrorCS", {"start": v(-15, -120) * mm, "end": v(-15, -108) * mm});
            skLineSegment(sketch, "E94.MirrorCS", {"start": v(15, -108) * mm, "end": v(33, -90) * mm});
            skArc(sketch, "E95.MirrorCS", {"start": v(-15, -120) * mm, "mid": v(0, -135) * mm, "end": v(15, -120) * mm});
            skLineSegment(sketch, "E96.MirrorCS", {"start": v(0, -90) * mm, "end": v(0, -120) * mm, "construction": true});
            skSolve(sketch);
        }
        {
            var Q0;
            Q0=makeQuery(id+"F16.imprint","IMPRINT",FACE,{"disambiguationData":[TD([[makeQuery(id+"F16.imprint","IMPRINT",EDGE,{"derivedFrom":makeQuery(id+"F1.opExtrude","CAP_EDGE",EDGE,{"disambiguationData":[OSD([sQuery(id+"F0.wireOp",EDGE,"E1.left")])],"isStart":true})}),-1.0]])]});
            var Q1;
            Q1=makeQuery(id+"F16.imprint","IMPRINT",FACE,{"disambiguationData":[TD([[makeQuery(id+"F16.imprint","IMPRINT",EDGE,{"derivedFrom":sQuery(id+"F16.wireOp",EDGE,"E84")}),-1.0]])]});
            var Q2;
            Q2=makeQuery(id+"F16.imprint","IMPRINT",FACE,{"disambiguationData":[TD([[makeQuery(id+"F16.imprint","IMPRINT",EDGE,{"derivedFrom":sQuery(id+"F16.wireOp",EDGE,"E88.MirrorCS")}),1.0]])]});
            var Q3;
            Q3=makeQuery(id+"F2.opExtrude","CAP_FACE",FACE,{"disambiguationData":[OSD([sQuery(id+"F0.wireOp",EDGE,"E12"),sQuery(id+"F0.wireOp",EDGE,"E13"),sQuery(id+"F0.wireOp",EDGE,"E14"),sQuery(id+"F0.wireOp",EDGE,"E15"),sQuery(id+"F0.wireOp",EDGE,"E17.filletArc"),sQuery(id+"F0.wireOp",EDGE,"E18.filletArc"),sQuery(id+"F0.wireOp",EDGE,"E19.filletArc"),sQuery(id+"F0.wireOp",EDGE,"E20.filletArc"),sQuery(id+"F0.wireOp",EDGE,"E25.0"),sQuery(id+"F0.wireOp",EDGE,"E25.1"),sQuery(id+"F0.wireOp",EDGE,"E25.2"),sQuery(id+"F0.wireOp",EDGE,"E25.3"),sQuery(id+"F0.wireOp",EDGE,"E25.4"),sQuery(id+"F0.wireOp",EDGE,"E25.5"),sQuery(id+"F0.wireOp",EDGE,"E25.6"),sQuery(id+"F0.wireOp",EDGE,"E25.7")])],"isStart":false});
            extrude(context, id + "F17", {"entities" : qUnion([Q0, Q1, Q2]), "endBound" : BoundingType.UP_TO_SURFACE, "endBoundEntityFace" : qUnion([Q3]), "depth" : 25 * mm});
        }
    });
